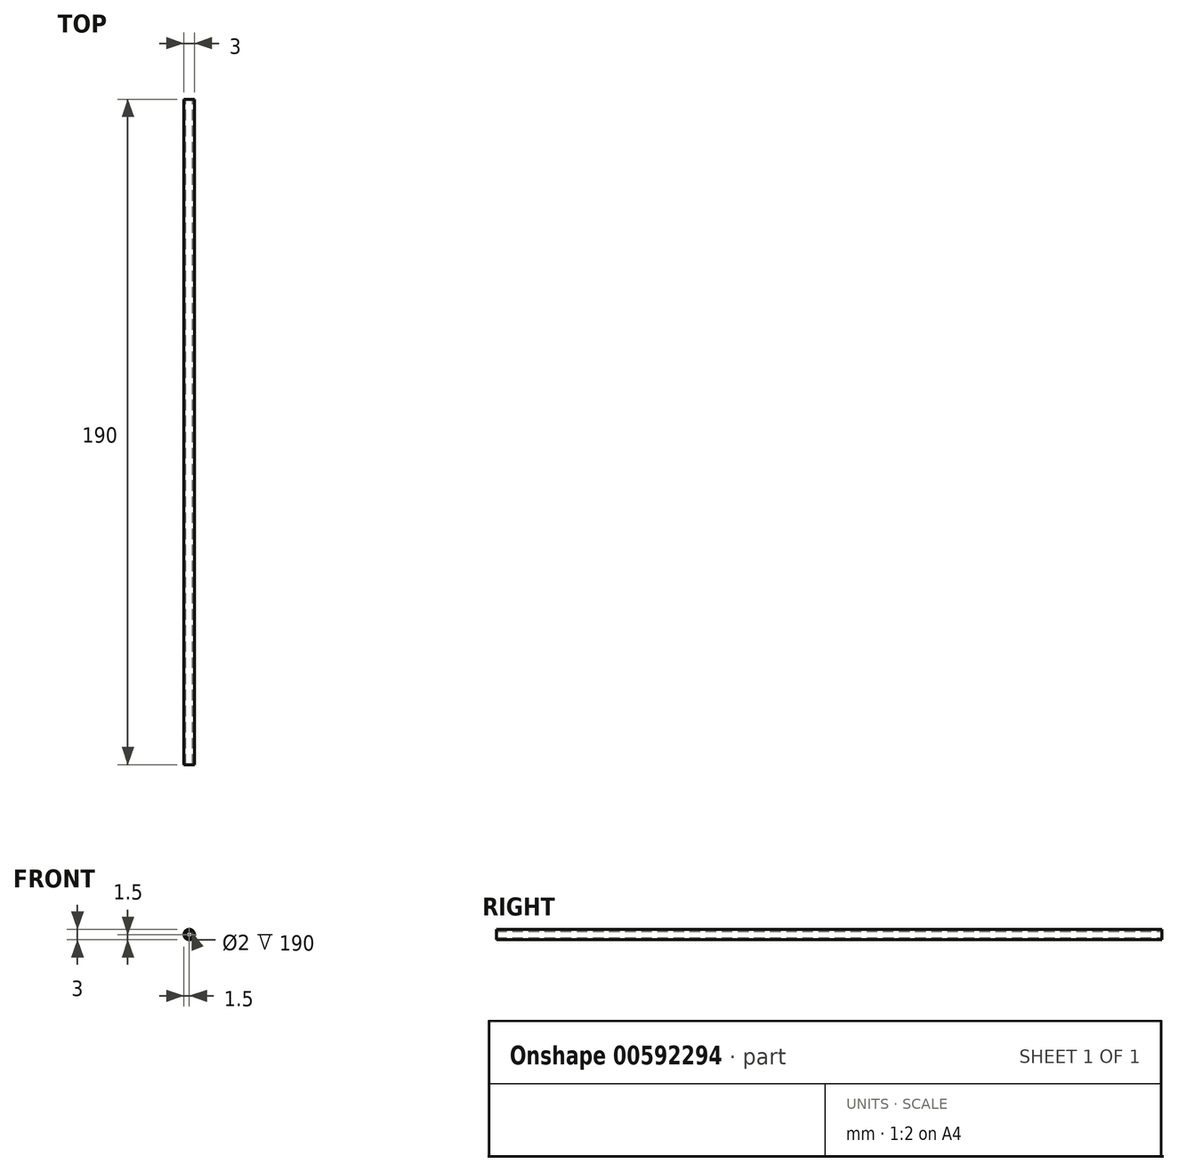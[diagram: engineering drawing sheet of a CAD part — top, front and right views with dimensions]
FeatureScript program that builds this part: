
annotation { "Feature Type Name" : "Feature", "Feature Type Description" : "" }
export const myFeature = defineFeature(function(context is Context, id is Id, definition is map)
    precondition{}
    {
        {
            var Q0;
            Q0=qCreatedBy(makeId("Front.planeOp"),FACE);
            var sketch = newSketch(context, id + "F0", { "sketchPlane" : qUnion([Q0])});
            skCircle(sketch, "E0", {"center": v(0, 0) * mm, "radius": 1.5 * mm});
            skCircle(sketch, "E1", {"center": v(0, 0) * mm, "radius": 1 * mm});
            skSolve(sketch);
        }
        {
            var Q0;
            Q0 = qSketchRegion(id + "F0", true);
            extrude(context, id + "F1", {"entities" : qUnion([Q0]), "depth" : 190 * mm, "offsetDistance" : 25 * mm});
        }
    });
